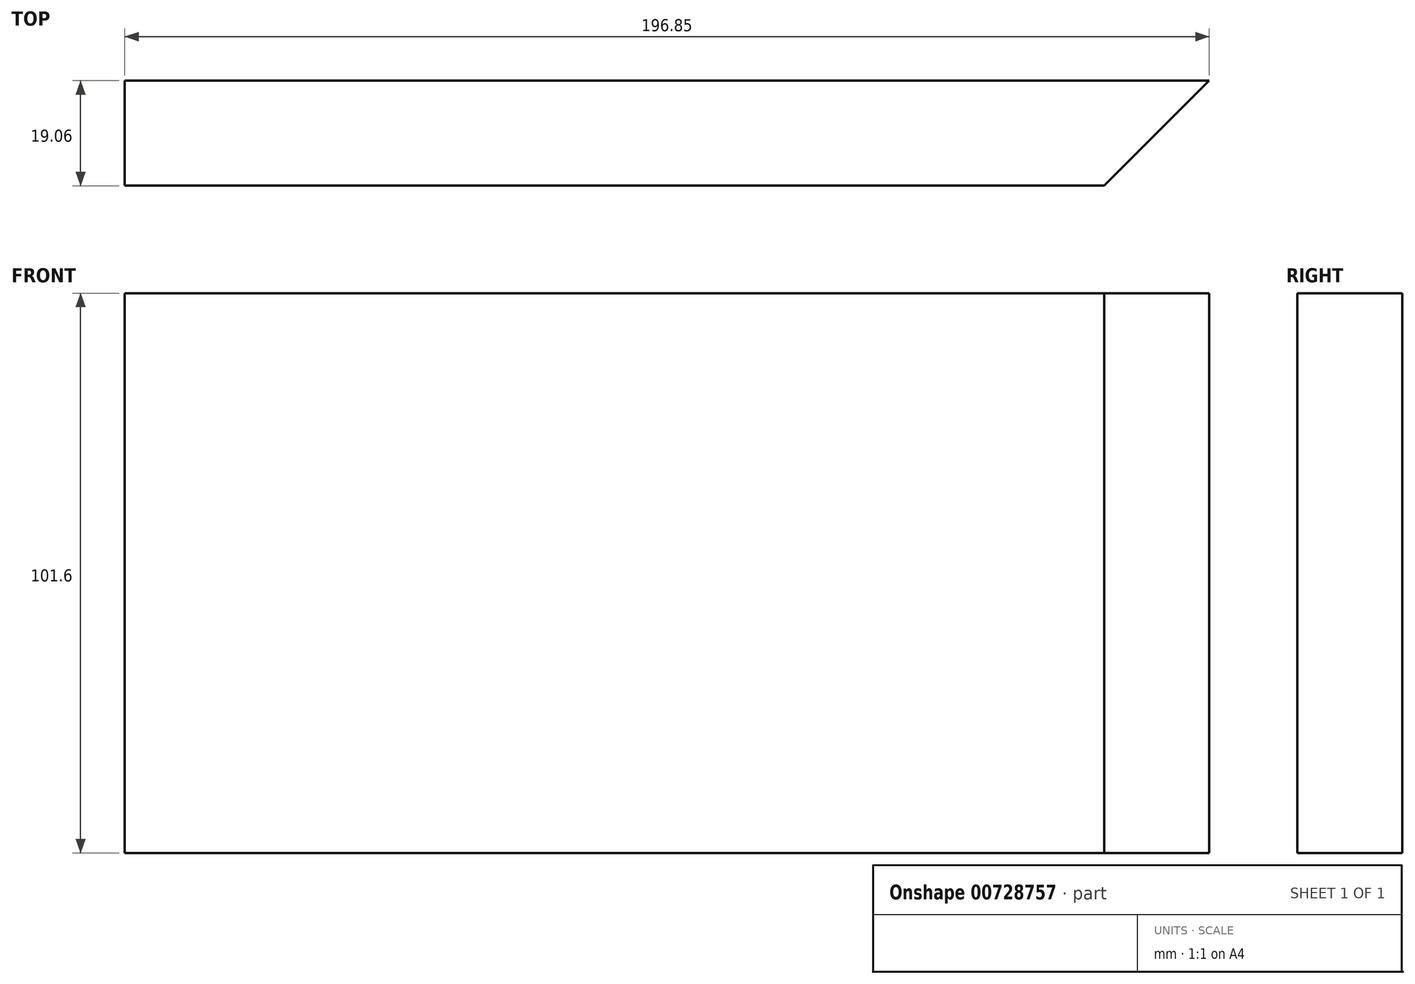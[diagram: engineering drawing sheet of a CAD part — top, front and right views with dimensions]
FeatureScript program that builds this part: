
annotation { "Feature Type Name" : "Feature", "Feature Type Description" : "" }
export const myFeature = defineFeature(function(context is Context, id is Id, definition is map)
    precondition{}
    {
        {
            var Q0;
            Q0=qCreatedBy(makeId("Right.planeOp"),FACE);
            var sketch = newSketch(context, id + "F0", { "sketchPlane" : qUnion([Q0])});
            skLineSegment(sketch, "E0.bottom", {"start": v(9.53, -50.8) * mm, "end": v(-9.52, -50.8) * mm});
            skLineSegment(sketch, "E0.top", {"start": v(9.53, 50.8) * mm, "end": v(-9.52, 50.8) * mm});
            skLineSegment(sketch, "E0.left", {"start": v(9.53, -50.8) * mm, "end": v(9.53, 50.8) * mm});
            skLineSegment(sketch, "E0.right", {"start": v(-9.52, -50.8) * mm, "end": v(-9.52, 50.8) * mm});
            skPoint(sketch, "E0.middle", {"position": v(0, 0) * mm});
            skSolve(sketch);
        }
        {
            var Q0;
            Q0 = qSketchRegion(id + "F0", true);
            extrude(context, id + "F1", {"entities" : qUnion([Q0]), "depth" : 19.05 * mm, "offsetDistance" : 25.4 * mm});
        }
        {
            var Q0;
            Q0 = qSketchRegion(id + "F0", true);
            extrude(context, id + "F2", {"entities" : qUnion([Q0]), "operationType" : NewBodyOperationType.ADD, "depth" : 196.85 * mm, "offsetDistance" : 25.4 * mm});
        }
        {
            var Q0;
            Q0=makeQuery(id+"F2.opExtrude","CAP_EDGE",EDGE,{"disambiguationData":[OSD([sQuery(id+"F0.wireOp",EDGE,"E0.right")])],"isStart":false});
            chamfer(context, id + "F3", {"entities" : qUnion([Q0]), "width" : 19.05 * mm, "tangentPropagation" : true});
        }
    });
